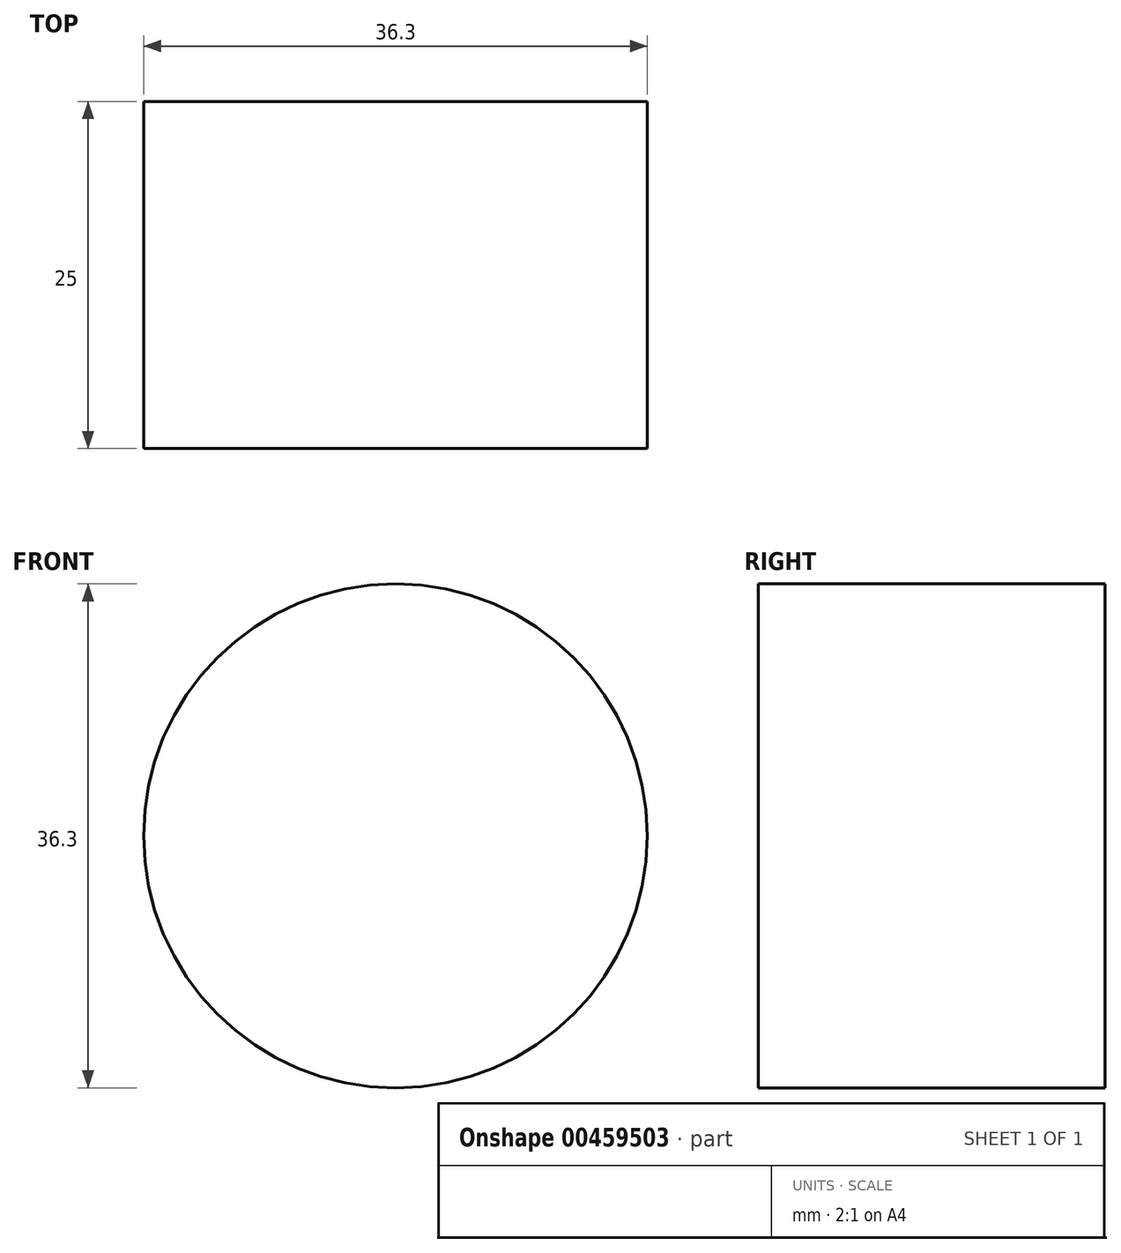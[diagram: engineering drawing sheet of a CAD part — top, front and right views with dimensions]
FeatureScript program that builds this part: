
annotation { "Feature Type Name" : "Feature", "Feature Type Description" : "" }
export const myFeature = defineFeature(function(context is Context, id is Id, definition is map)
    precondition{}
    {
        {
            var Q0;
            Q0=qCreatedBy(makeId("Front.planeOp"),FACE);
            var sketch = newSketch(context, id + "F0", { "sketchPlane" : qUnion([Q0])});
            skCircle(sketch, "E0", {"center": v(0, 0) * mm, "radius": 18.15 * mm});
            skSolve(sketch);
        }
        {
            var Q0;
            Q0=makeQuery(id+"F0.imprint","IMPRINT",FACE,{"disambiguationData":[TD([[makeQuery(id+"F0.imprint","IMPRINT",EDGE,{"derivedFrom":sQuery(id+"F0.wireOp",EDGE,"E0")}),1.0]])]});
            extrude(context, id + "F1", {"entities" : qUnion([Q0]), "depth" : 25 * mm});
        }
    });
